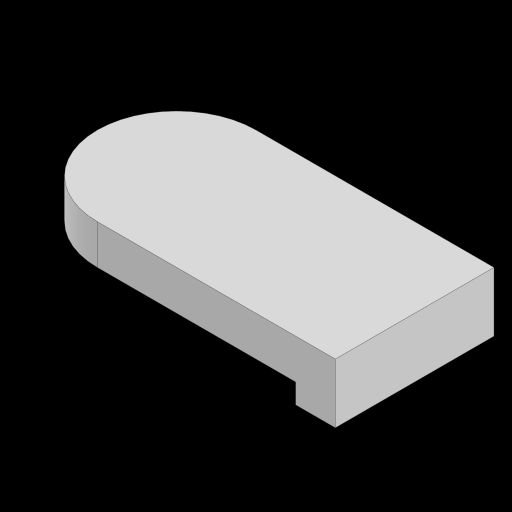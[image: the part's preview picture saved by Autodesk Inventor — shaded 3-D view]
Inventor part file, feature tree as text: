
AUTODESK INVENTOR PART (.ipt)
format: ipt  version: 2024 (Build 280153000, 153)  size: 97,792 bytes
history: native  units: in
note: dims shown in document units (in); Inventor stores cm internally (conversion verified against a paired STEP export)
features: extrude x2, sketch x2
ambient origin geometry x8: Origin, YZ Plane, XZ Plane, XY Plane, X Axis, Y Axis, Z Axis, Center Point
bodies: Solid1 (feature_tree)
feature tree (4):
  extrude  "Extrusion1"  Depth=2.0in
  extrude  "Extrusion2"  Depth=0.25in
  sketch  "Sketch1"  dims[d0=2.0in d1=3.0in]
  sketch  "Sketch2"  dims[d2=0.5in d3=0.0in d4=0.25in d5=0.5in d6=0.0in]
